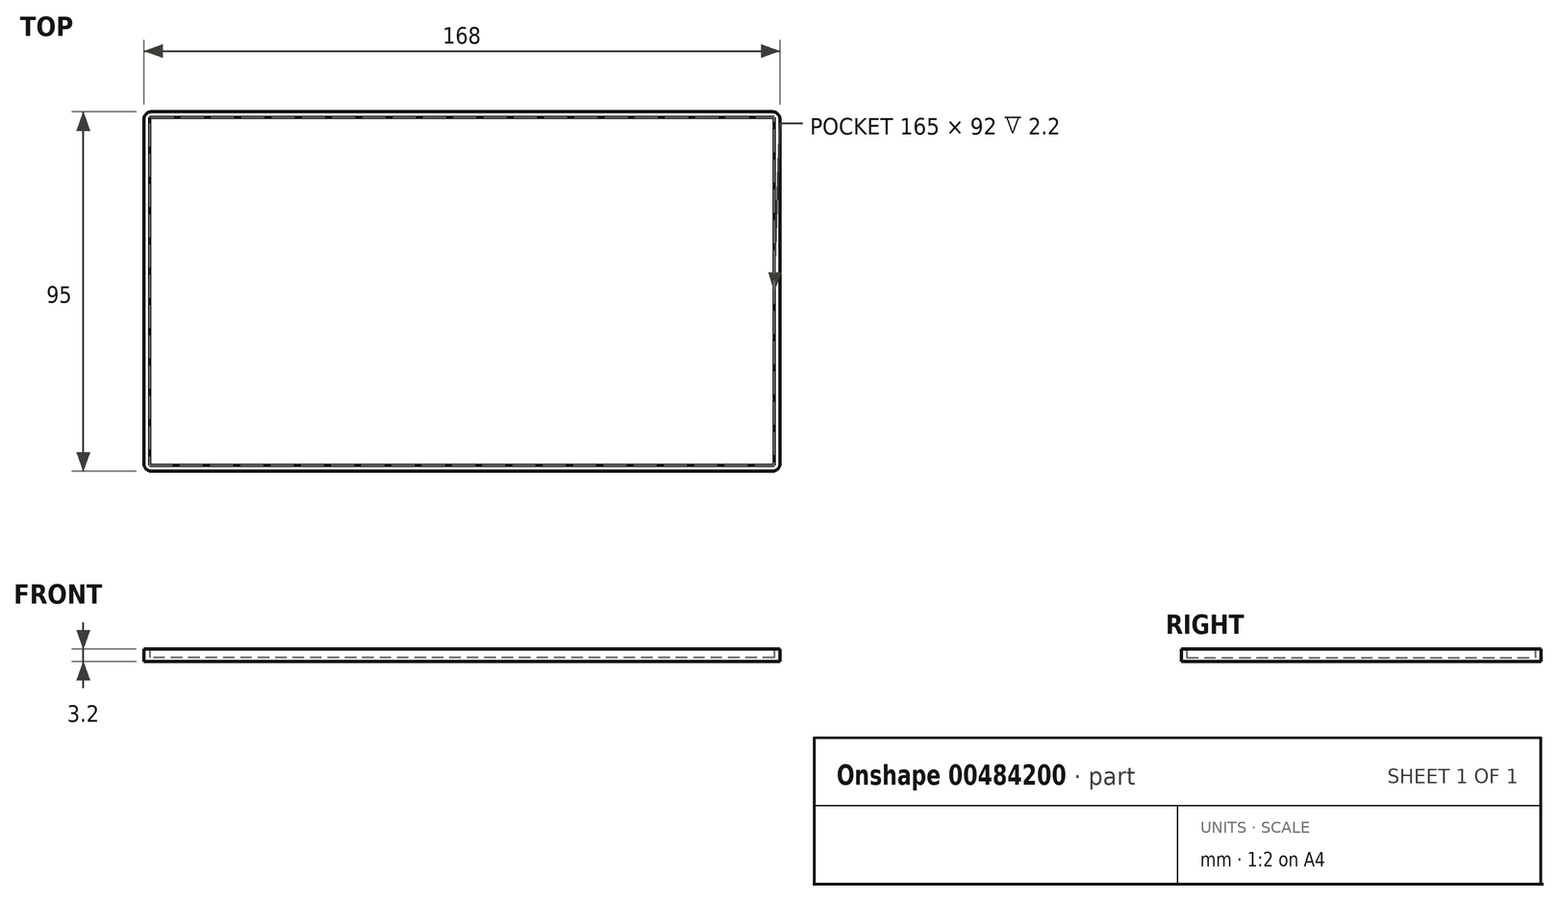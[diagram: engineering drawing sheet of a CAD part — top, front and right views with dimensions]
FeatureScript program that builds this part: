
annotation { "Feature Type Name" : "Feature", "Feature Type Description" : "" }
export const myFeature = defineFeature(function(context is Context, id is Id, definition is map)
    precondition{}
    {
        {
            var Q0;
            Q0=qCreatedBy(makeId("Top.planeOp"),FACE);
            var sketch = newSketch(context, id + "F0", { "sketchPlane" : qUnion([Q0])});
            skLineSegment(sketch, "E0.bottom", {"start": v(82.5, -46) * mm, "end": v(-82.5, -46) * mm});
            skLineSegment(sketch, "E0.top", {"start": v(82.5, 46) * mm, "end": v(-82.5, 46) * mm});
            skLineSegment(sketch, "E0.left", {"start": v(82.5, -46) * mm, "end": v(82.5, 46) * mm});
            skLineSegment(sketch, "E0.right", {"start": v(-82.5, -46) * mm, "end": v(-82.5, 46) * mm});
            skPoint(sketch, "E0.middle", {"position": v(0, 0) * mm});
            skLineSegment(sketch, "E1.0", {"start": v(-84, -47.5) * mm, "end": v(-84, 47.5) * mm});
            skLineSegment(sketch, "E1.1", {"start": v(84, -47.5) * mm, "end": v(-84, -47.5) * mm});
            skLineSegment(sketch, "E1.2", {"start": v(84, -47.5) * mm, "end": v(84, 47.5) * mm});
            skLineSegment(sketch, "E1.3", {"start": v(84, 47.5) * mm, "end": v(-84, 47.5) * mm});
            skSolve(sketch);
        }
        {
            var Q0;
            Q0=makeQuery(id+"F0.imprint","IMPRINT",FACE,{"disambiguationData":[TD([[makeQuery(id+"F0.imprint","IMPRINT",EDGE,{"derivedFrom":sQuery(id+"F0.wireOp",EDGE,"E0.bottom")}),1.0]])]});
            extrude(context, id + "F1", {"entities" : qUnion([Q0]), "depth" : 2.2 * mm});
        }
        {
            var Q0;
            Q0=makeQuery(id+"F1.opExtrude","CAP_FACE",FACE,{"disambiguationData":[OSD([sQuery(id+"F0.wireOp",EDGE,"E0.bottom"),sQuery(id+"F0.wireOp",EDGE,"E0.top"),sQuery(id+"F0.wireOp",EDGE,"E0.left"),sQuery(id+"F0.wireOp",EDGE,"E0.right"),sQuery(id+"F0.wireOp",EDGE,"E1.0"),sQuery(id+"F0.wireOp",EDGE,"E1.1"),sQuery(id+"F0.wireOp",EDGE,"E1.2"),sQuery(id+"F0.wireOp",EDGE,"E1.3")])],"isStart":true});
            var Q1;
            Q1=makeQuery(id+"F0.imprint","IMPRINT",FACE,{"disambiguationData":[TD([[makeQuery(id+"F0.imprint","IMPRINT",EDGE,{"derivedFrom":sQuery(id+"F0.wireOp",EDGE,"E0.bottom")}),-1.0]])]});
            extrude(context, id + "F2", {"entities" : qUnion([Q0, Q1]), "operationType" : NewBodyOperationType.ADD, "depth" : 1 * mm});
        }
        {
            var Q0;
            {var subQ0=sQuery(id+"F0.wireOp",EDGE,"E1.1");var subQ1=sQuery(id+"F0.wireOp",EDGE,"E1.0");Q0=makeQuery(id+"F2.boolean.opBoolean","MERGE",EDGE,{"derivedFrom":[makeQuery(id+"F1.opExtrude","SWEPT_EDGE",EDGE,{"disambiguationData":[OSD([subQ1,subQ0])]}),makeQuery(id+"F2.opExtrude","SWEPT_EDGE",EDGE,{"disambiguationData":[OSD([subQ1,subQ0])]})]});}
            var Q1;
            {var subQ0=sQuery(id+"F0.wireOp",EDGE,"E1.3");var subQ1=sQuery(id+"F0.wireOp",EDGE,"E1.0");Q1=makeQuery(id+"F2.boolean.opBoolean","MERGE",EDGE,{"derivedFrom":[makeQuery(id+"F1.opExtrude","SWEPT_EDGE",EDGE,{"disambiguationData":[OSD([subQ1,subQ0])]}),makeQuery(id+"F2.opExtrude","SWEPT_EDGE",EDGE,{"disambiguationData":[OSD([subQ1,subQ0])]})]});}
            var Q2;
            {var subQ0=sQuery(id+"F0.wireOp",EDGE,"E1.2");var subQ1=sQuery(id+"F0.wireOp",EDGE,"E1.1");Q2=makeQuery(id+"F2.boolean.opBoolean","MERGE",EDGE,{"derivedFrom":[makeQuery(id+"F1.opExtrude","SWEPT_EDGE",EDGE,{"disambiguationData":[OSD([subQ1,subQ0])]}),makeQuery(id+"F2.opExtrude","SWEPT_EDGE",EDGE,{"disambiguationData":[OSD([subQ1,subQ0])]})]});}
            var Q3;
            {var subQ0=sQuery(id+"F0.wireOp",EDGE,"E1.3");var subQ1=sQuery(id+"F0.wireOp",EDGE,"E1.2");Q3=makeQuery(id+"F2.boolean.opBoolean","MERGE",EDGE,{"derivedFrom":[makeQuery(id+"F1.opExtrude","SWEPT_EDGE",EDGE,{"disambiguationData":[OSD([subQ1,subQ0])]}),makeQuery(id+"F2.opExtrude","SWEPT_EDGE",EDGE,{"disambiguationData":[OSD([subQ1,subQ0])]})]});}
            fillet(context, id + "F3", {"entities" : qUnion([Q0, Q1, Q2, Q3]), "radius" : 2 * mm, "tangentPropagation" : true, "allowEdgeOverflow" : false});
        }
    });
